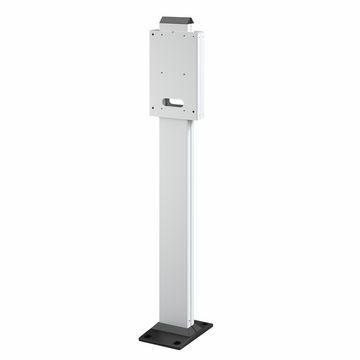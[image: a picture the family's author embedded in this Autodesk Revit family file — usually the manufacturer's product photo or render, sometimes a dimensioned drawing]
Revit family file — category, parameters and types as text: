
# Revit family: Building-ElectricalVehicleCharging-GEWISS-JOINON-ICON_2-SIDED-FLOOR-MOUNT-SUPPORT
name_source: partatom
category: Apparecchi elettrici
units: mm (PartAtom-declared; Revit-internal decimal feet)

## family parameters
Condiviso = No
Host = Superficie
Mantenere orientamento annotazione = Sì
Punto di calcolo locali = Sì
Quota connettore circolare = Usa diametro
Taglio con vuoti quando caricato = No
Tipo di parte = Normale

## types (1)
- GWJ8103 - I-CON - TWO-SIDED FLOOR-MOUNTING SUPPORT
    BLOCCO = B=C
    Catalogue = E-MOBILITY
    Description: = I-CON floor-mounting support - double-sided
    Descrizione = I-CON - TWO-SIDED FLOOR-MOUNTING SUPPORT
    EAN code = 8034035071386
    Electrocod = 2242
    FORMULA = 1000 mm  [stored 3.28084 ft]
    IDF = 20ef0ad5-a66f-4bfd-9742-53af65c7bb1f
    IDT = c8e419b7-85e3-4455-b847-1a1252f0ba31
    Immagine tipo = ICON_SUPP_BI.jpg
    L = 155 mm  [stored 0.50853 ft]
    Modello = GWJ8103
    N.poli = 1
    POMELLO = bianco
    PRESA = Giallo
    Produttore = GEWISS S.p.A.
    Prospetto di default = 1219 mm
    STRUTTURA = RAL - 7035
    STRUTTURA ALTA = blue
    Spostamento_S = 1500 mm  [stored 4.92126 ft]
    Suitable for = WallBox I-CON
    Technical sheet = https://www.gewiss.com
    URL = https://www.gewiss.com
    VETRO = Vetro
    Version file RFA = 19.4
    Voltaggio = 0 V
    W = 115 mm  [stored 0.377297 ft]

note: [stored X ft] marks values corroborated as IEEE doubles in the binary element streams (Revit-internal decimal feet)
